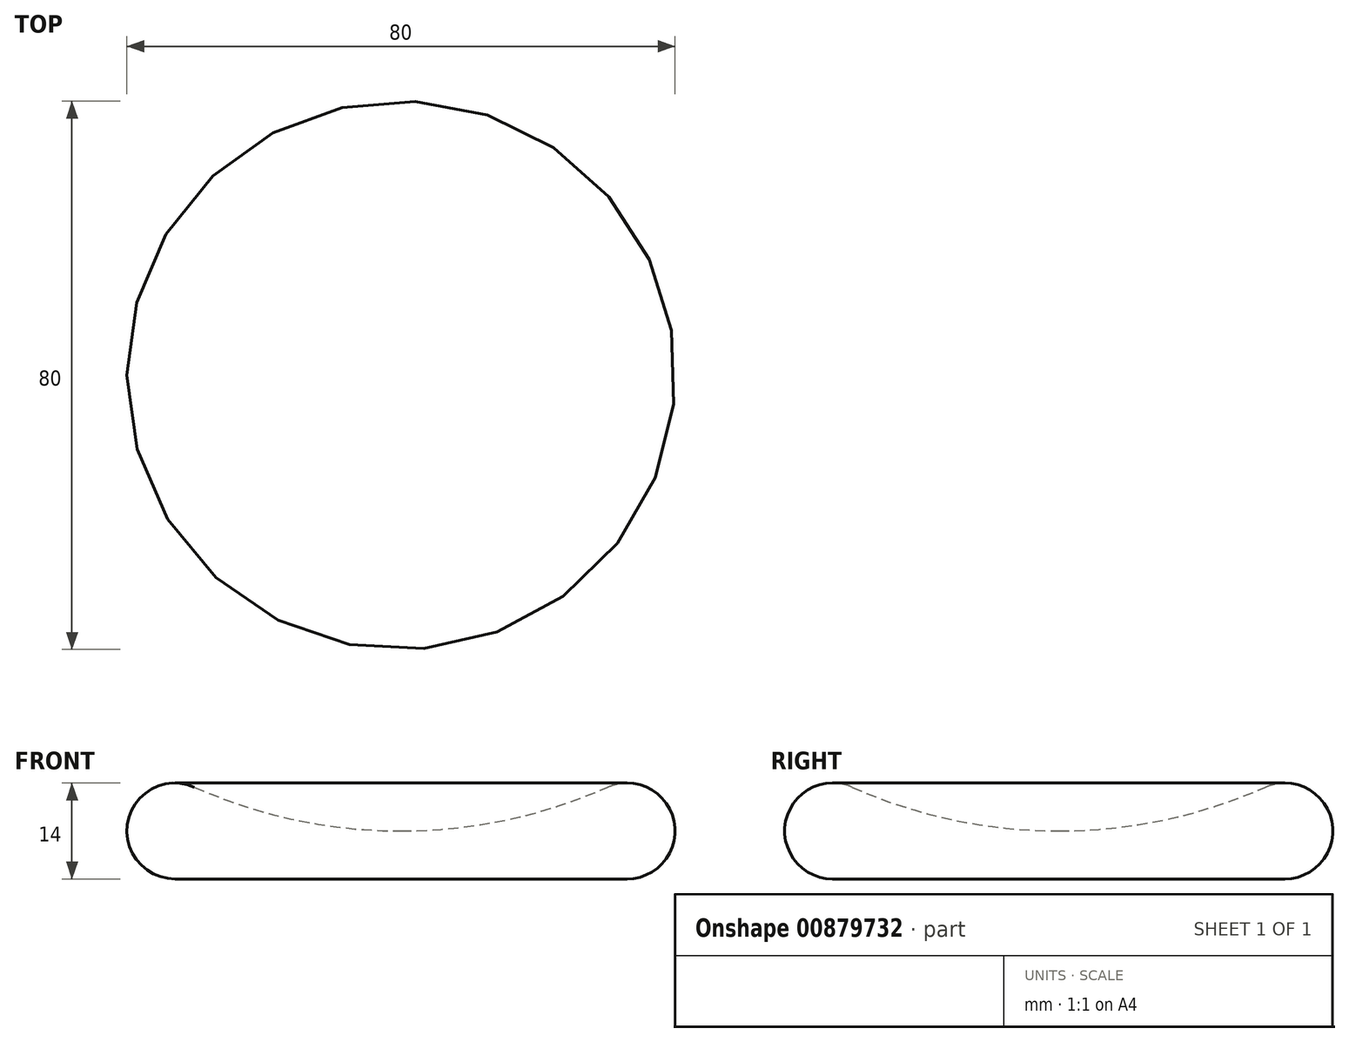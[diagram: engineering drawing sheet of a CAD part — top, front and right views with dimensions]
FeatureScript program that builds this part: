
annotation { "Feature Type Name" : "Feature", "Feature Type Description" : "" }
export const myFeature = defineFeature(function(context is Context, id is Id, definition is map)
    precondition{}
    {
        {
            var Q0;
            Q0=qCreatedBy(makeId("Front.planeOp"),FACE);
            var sketch = newSketch(context, id + "F0", { "sketchPlane" : qUnion([Q0])});
            skArc(sketch, "E0", {"start": v(-30.16, 13.4) * mm, "mid": v(-39.85, 8.45) * mm, "end": v(-33, 0) * mm});
            skArc(sketch, "E1", {"start": v(-30.16, 13.4) * mm, "mid": v(-15.41, 8.62) * mm, "end": v(0, 7) * mm});
            skLineSegment(sketch, "E2", {"start": v(0, 0) * mm, "end": v(-33, 0) * mm});
            skLineSegment(sketch, "E3", {"start": v(-33, 0) * mm, "end": v(0, 0) * mm});
            skLineSegment(sketch, "E4", {"start": v(0, 0) * mm, "end": v(0, 7) * mm});
            skSolve(sketch);
        }
        {
            var Q0;
            Q0=makeQuery(id+"F0.imprint","IMPRINT",FACE,{"disambiguationData":[TD([[makeQuery(id+"F0.imprint","IMPRINT",EDGE,{"derivedFrom":sQuery(id+"F0.wireOp",EDGE,"E0")}),1.0]])]});
            var Q1;
            Q1=sQuery(id+"F0.wireOp",EDGE,"E4");
            revolve(context, id + "F1", {"surfaceOperationType" : NewSurfaceOperationType.NEW, "entities" : qUnion([Q0]), "axis" : qUnion([Q1]), "revolveType" : RevolveType.FULL});
        }
    });
